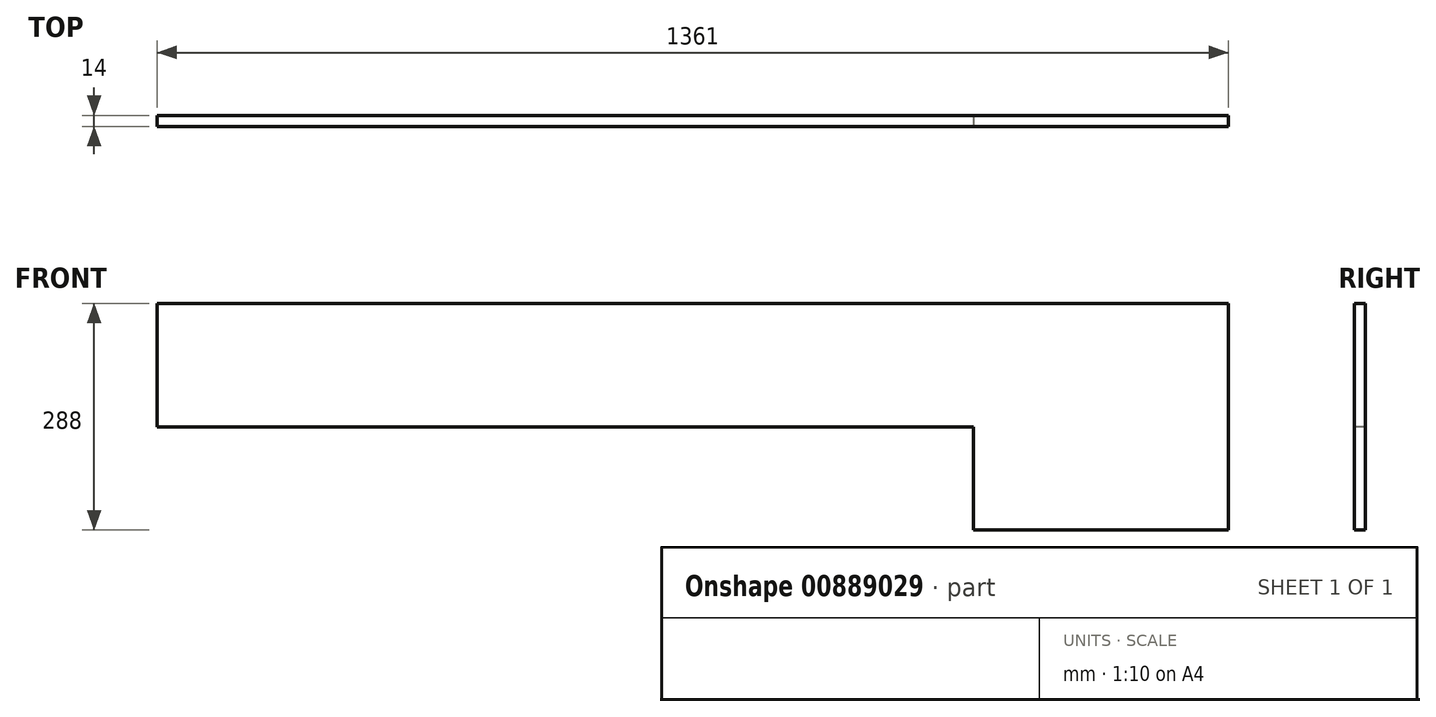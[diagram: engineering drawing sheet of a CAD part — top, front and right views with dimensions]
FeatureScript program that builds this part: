
annotation { "Feature Type Name" : "Feature", "Feature Type Description" : "" }
export const myFeature = defineFeature(function(context is Context, id is Id, definition is map)
    precondition{}
    {
        {
            var Q0;
            Q0=qCreatedBy(makeId("Right.planeOp"),FACE);
            var sketch = newSketch(context, id + "F0", { "sketchPlane" : qUnion([Q0])});
            skLineSegment(sketch, "E0.bottom", {"start": v(-7, 144) * mm, "end": v(7, 144) * mm});
            skLineSegment(sketch, "E0.top", {"start": v(-7, -144) * mm, "end": v(7, -144) * mm});
            skLineSegment(sketch, "E0.left", {"start": v(-7, 144) * mm, "end": v(-7, -144) * mm});
            skLineSegment(sketch, "E0.right", {"start": v(7, 144) * mm, "end": v(7, -144) * mm});
            skPoint(sketch, "E0.middle", {"position": v(0, 0) * mm});
            skSolve(sketch);
        }
        {
            var Q0;
            Q0=qSketchRegion(id+"F0",true);
            extrude(context, id + "F1", {"entities" : qUnion([Q0]), "endBound" : BoundingType.SYMMETRIC, "depth" : 1361 * mm, "offsetDistance" : 25 * mm});
        }
        {
            var Q0;
            Q0=makeQuery(id+"F1.opExtrude","SWEPT_FACE",FACE,{"disambiguationData":[OSD([sQuery(id+"F0.wireOp",EDGE,"E0.left")])]});
            var sketch = newSketch(context, id + "F2", { "sketchPlane" : qUnion([Q0])});
            skLineSegment(sketch, "E1.bottom", {"start": v(-680.5, -144) * mm, "end": v(356.5, -144) * mm});
            skLineSegment(sketch, "E1.top", {"start": v(-680.5, -13) * mm, "end": v(356.5, -13) * mm});
            skLineSegment(sketch, "E1.left", {"start": v(-680.5, -144) * mm, "end": v(-680.5, -13) * mm});
            skLineSegment(sketch, "E1.right", {"start": v(356.5, -144) * mm, "end": v(356.5, -13) * mm});
            skSolve(sketch);
        }
        {
            var Q0;
            Q0 = qSketchRegion(id + "F2", true);
            extrude(context, id + "F3", {"entities" : qUnion([Q0]), "operationType" : NewBodyOperationType.REMOVE, "oppositeDirection" : true, "depth" : 25 * mm, "offsetDistance" : 25 * mm});
        }
    });
